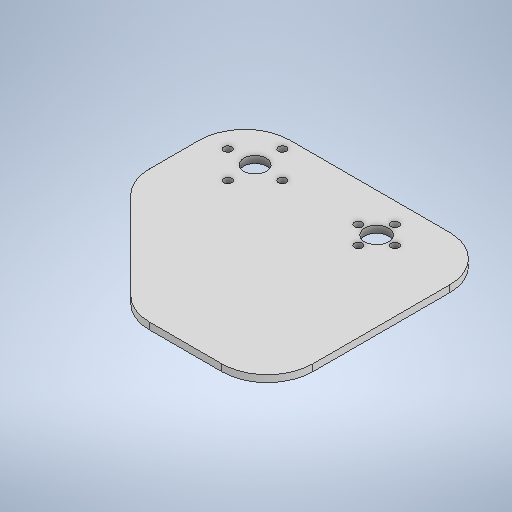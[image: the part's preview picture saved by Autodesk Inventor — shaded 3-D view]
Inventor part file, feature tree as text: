
AUTODESK INVENTOR PART (.ipt)
format: ipt  version: 2025.2 (Build 292293000, 293)  size: 272,896 bytes
history: native  units: mm
features: sketch x4, extrude x2, fillet x1
ambient origin geometry x8: Origin, YZ Plane, XZ Plane, XY Plane, X Axis, Y Axis, Z Axis, Center Point
bodies: Solid1 (feature_tree)
feature tree (7):
  extrude  "Extrusion1"  Depth=50.0mm
  extrude  "Extrusion6"  Depth=3.0mm
  fillet  "Fillet1"  Radius=10.5mm
  sketch  "Sketch1"  dims[d0=150.0mm d1=50.0mm]
  sketch  "Sketch6"  dims[d43=10.0mm d44=3.5mm d45=40.0mm d47=360.0deg d49=24.0mm d50=3.5mm d51=40.0mm d53=360.0deg d55=0.0mm d56=0.0mm d57=40.0mm d58=50.0mm d59=50.0mm d60=60.0mm d61=20.0mm d26=0.5mm d27=0.872665mm d28=0.5mm d29=0.872665mm]
  sketch  "Sketch Circular Pattern1"  dims[d2=3.0mm d3=0.0mm d40=17.0mm d41=10.5mm]
  sketch  "Sketch Circular Pattern2"  dims[d42=53.4mm]
